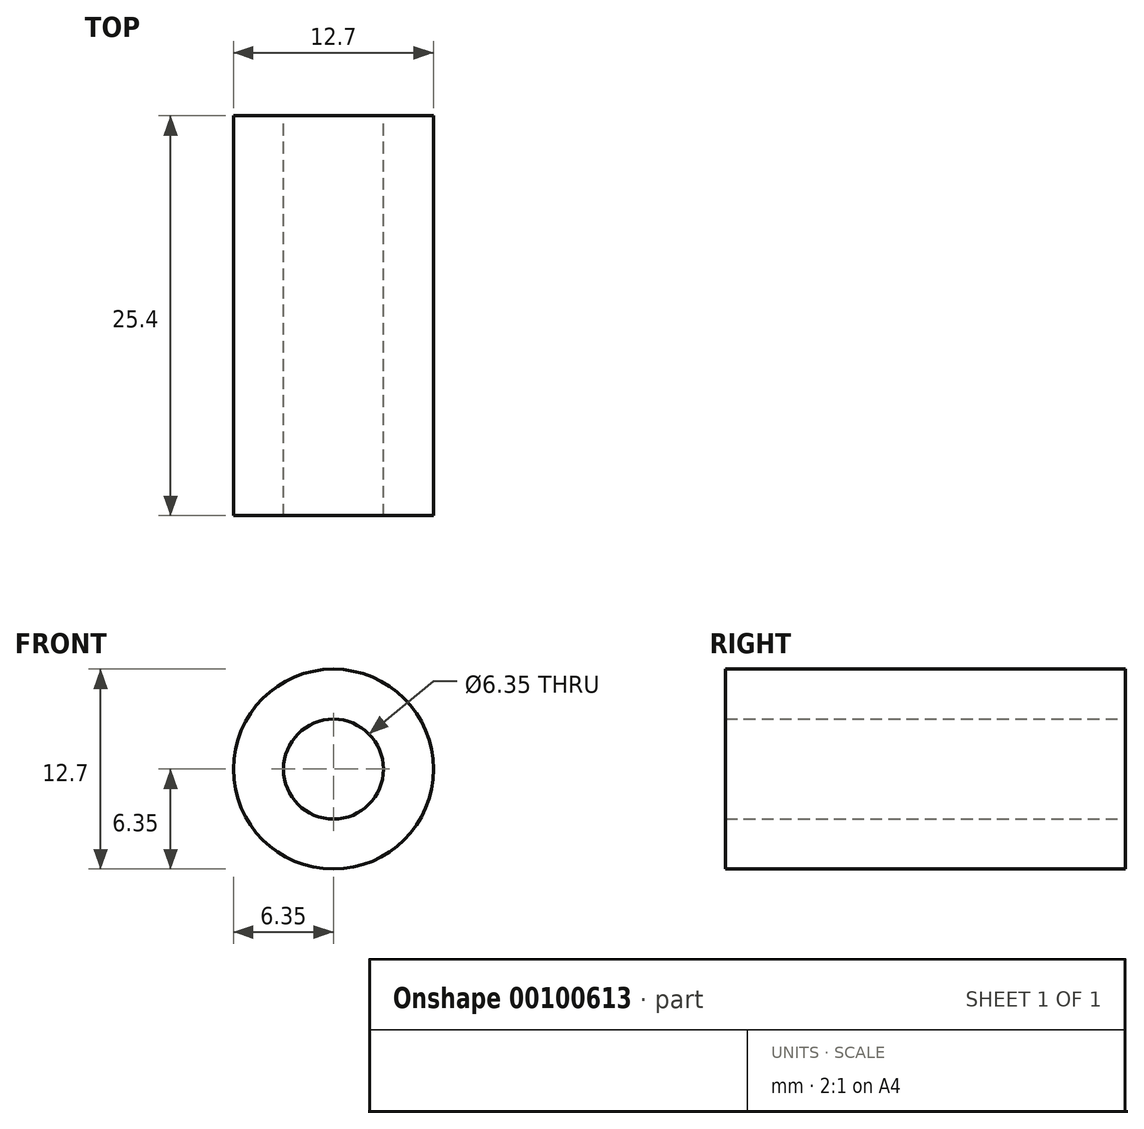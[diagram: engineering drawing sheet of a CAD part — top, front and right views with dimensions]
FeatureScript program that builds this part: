
annotation { "Feature Type Name" : "Feature", "Feature Type Description" : "" }
export const myFeature = defineFeature(function(context is Context, id is Id, definition is map)
    precondition{}
    {
        {
            var Q0;
            Q0=qCreatedBy(makeId("Front.planeOp"),FACE);
            var sketch = newSketch(context, id + "F0", { "sketchPlane" : qUnion([Q0])});
            skCircle(sketch, "E0", {"center": v(0, 0) * mm, "radius": 3.17 * mm});
            skCircle(sketch, "E1", {"center": v(0, 0) * mm, "radius": 6.35 * mm});
            skSolve(sketch);
        }
        {
            var Q0;
            Q0=makeQuery(id+"F0.imprint","IMPRINT",FACE,{"disambiguationData":[TD([[makeQuery(id+"F0.imprint","IMPRINT",EDGE,{"derivedFrom":sQuery(id+"F0.wireOp",EDGE,"E0")}),-1.0]])]});
            extrude(context, id + "F1", {"entities" : qUnion([Q0]), "depth" : 25.4 * mm});
        }
    });
